# Revit family: Gira_2280005
name_source: partatom
category: Electrical Fixtures
revit_build: Autodesk Revit 2017 (Build: 20160225_1515(x64)
units: mm (PartAtom-declared; Revit-internal decimal feet)

## family parameters
Cut with Voids When Loaded = No
Host = Face
Maintain Annotation Orientation = Yes
Part Type = Normal
Room Calculation Point = No
Round Connector Dimension = Use Diameter
Shared = No

## types (1)
- UP-Radio RDS Lautsprecher System 55 Schwarz m
    Ausführung = Radio (*en-EN)
    Ausführung der Oberfläche = matt
    Available = Yes
    Befestigungsart = Krallen-/Schraubbefestigung
    Category = Elektronik-Gerät für Installationsschalterprogramme
    Data sheet (1) = https://katalog.gira.de
    Default Elevation = 1219 mm
    Farbe = schwarz
    GTIN = 4010337038054
    HAN = 2280005
    Halogenfrei = No
    HeinzeBIM = https://bimportal.heinze.de
    Keynote = Sys55_Komplettgerät_UP-Radio
    Manufacturer URL = https://www.gira.de
    Montageart = unter Putz
    Name = UP-Radio RDS Lautsprecher System 55 Schwarz m
    Oberfläche = sonstige
    Region = DE
    Transparent = No
    URL = http://katalog.gira.de
    Werkstoff = sonstige
    Werkstoffgüte = sonstige
    Zusammenstellung = Basiselement

## geometry (parser evidence)
native form markers: Blend x2, Sweep x2
no freeform markers — native parametric forms only
